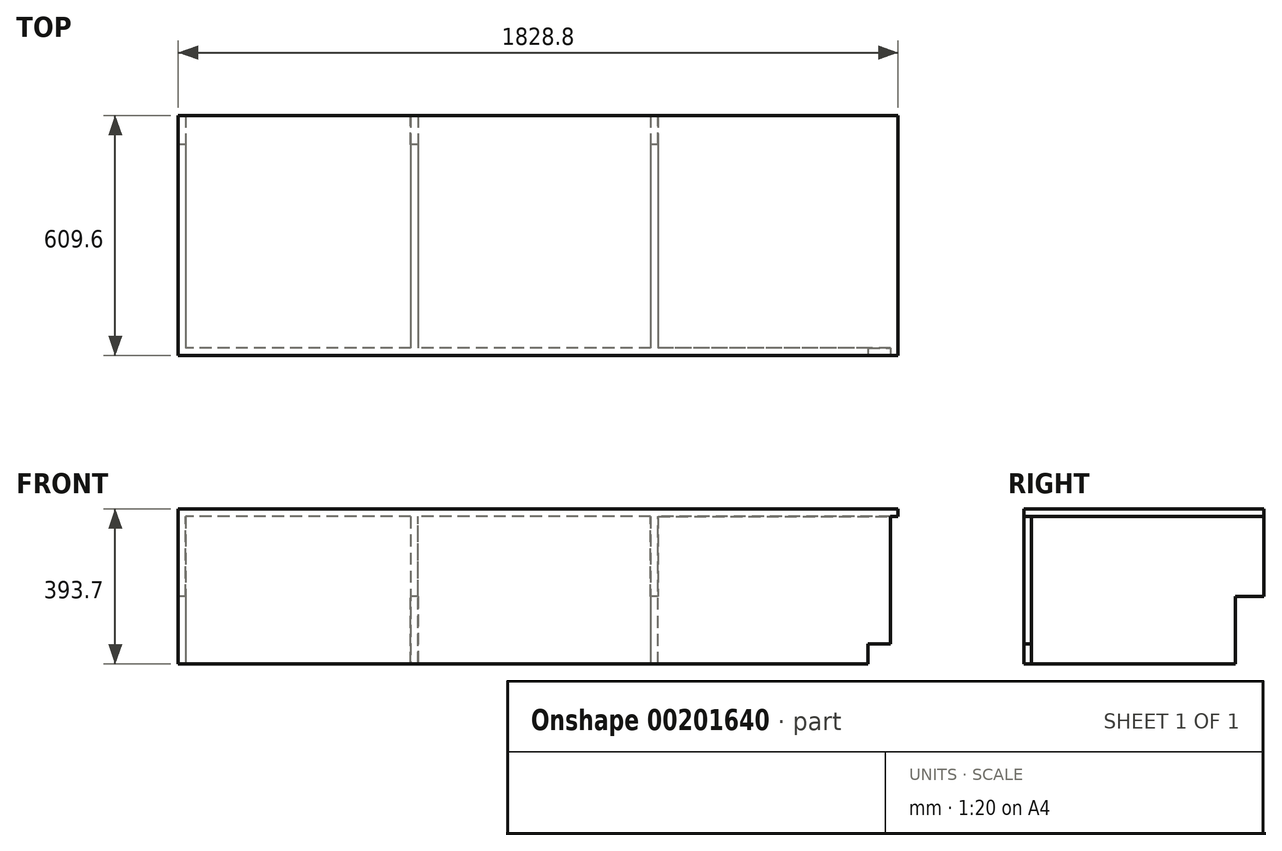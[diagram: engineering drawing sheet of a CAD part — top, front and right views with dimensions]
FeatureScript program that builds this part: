
annotation { "Feature Type Name" : "Feature", "Feature Type Description" : "" }
export const myFeature = defineFeature(function(context is Context, id is Id, definition is map)
    precondition{}
    {
        {
            var Q0;
            Q0=qCreatedBy(makeId("Front.planeOp"),FACE);
            var sketch = newSketch(context, id + "F0", { "sketchPlane" : qUnion([Q0])});
            skLineSegment(sketch, "E0", {"start": v(0, 0) * mm, "end": v(0, 50.8) * mm});
            skLineSegment(sketch, "E1", {"start": v(0, 50.8) * mm, "end": v(76.2, 50.8) * mm});
            skLineSegment(sketch, "E2", {"start": v(76.2, 50.8) * mm, "end": v(76.2, 374.65) * mm});
            skLineSegment(sketch, "E3", {"start": v(0, 0) * mm, "end": v(-1752.6, 0) * mm});
            skLineSegment(sketch, "E4", {"start": v(-1752.6, 0) * mm, "end": v(-1752.6, 374.65) * mm});
            skLineSegment(sketch, "E5.bottom", {"start": v(-1752.6, 374.65) * mm, "end": v(76.2, 374.65) * mm});
            skLineSegment(sketch, "E5.top", {"start": v(-1752.6, 393.7) * mm, "end": v(76.2, 393.7) * mm});
            skLineSegment(sketch, "E5.left", {"start": v(-1752.6, 374.65) * mm, "end": v(-1752.6, 393.7) * mm});
            skLineSegment(sketch, "E5.right", {"start": v(76.2, 374.65) * mm, "end": v(76.2, 393.7) * mm});
            skLineSegment(sketch, "E6.bottom", {"start": v(76.2, 374.65) * mm, "end": v(57.15, 374.65) * mm});
            skLineSegment(sketch, "E6.top", {"start": v(76.2, 50.8) * mm, "end": v(57.15, 50.8) * mm});
            skLineSegment(sketch, "E6.left", {"start": v(76.2, 374.65) * mm, "end": v(76.2, 50.8) * mm});
            skLineSegment(sketch, "E6.right", {"start": v(57.15, 374.65) * mm, "end": v(57.15, 50.8) * mm});
            skLineSegment(sketch, "E7", {"start": v(-533.4, 374.65) * mm, "end": v(-533.4, 0) * mm});
            skLineSegment(sketch, "E8", {"start": v(-533.4, 0) * mm, "end": v(-552.45, 0) * mm});
            skLineSegment(sketch, "E9", {"start": v(-552.45, 0) * mm, "end": v(-552.45, 374.65) * mm});
            skLineSegment(sketch, "E10", {"start": v(-1143, 0) * mm, "end": v(-1143, 374.65) * mm});
            skLineSegment(sketch, "E11", {"start": v(-1162.05, 374.65) * mm, "end": v(-1162.05, 0) * mm});
            skLineSegment(sketch, "E12", {"start": v(-1733.55, 0) * mm, "end": v(-1733.55, 374.65) * mm});
            skSolve(sketch);
        }
        {
            var Q0;
            {var subQ0=sQuery(id+"F0.wireOp",EDGE,"E4");Q0=makeQuery(id+"F0.imprint","IMPRINT",FACE,{"disambiguationData":[TD([[makeQuery(id+"F0.imprint","IMPRINT",EDGE,{"derivedFrom":subQ0}),-1.0]])]});}
            var Q1;
            Q1=makeQuery(id+"F0.imprint","IMPRINT",FACE,{"disambiguationData":[TD([[makeQuery(id+"F0.imprint","IMPRINT",EDGE,{"derivedFrom":sQuery(id+"F0.wireOp",EDGE,"E5.top")}),-1.0]])]});
            var Q2;
            {var subQ0=sQuery(id+"F0.wireOp",EDGE,"E10");Q2=makeQuery(id+"F0.imprint","IMPRINT",FACE,{"disambiguationData":[TD([[makeQuery(id+"F0.imprint","IMPRINT",EDGE,{"derivedFrom":subQ0}),1.0]])]});}
            var Q3;
            {var subQ0=sQuery(id+"F0.wireOp",EDGE,"E7");Q3=makeQuery(id+"F0.imprint","IMPRINT",FACE,{"disambiguationData":[TD([[makeQuery(id+"F0.imprint","IMPRINT",EDGE,{"derivedFrom":subQ0}),-1.0]])]});}
            var Q4;
            Q4=makeQuery(id+"F0.imprint","IMPRINT",FACE,{"disambiguationData":[TD([[makeQuery(id+"F0.imprint","IMPRINT",EDGE,{"derivedFrom":sQuery(id+"F0.wireOp",EDGE,"E6.bottom")}),1.0]])]});
            extrude(context, id + "F1", {"entities" : qUnion([Q0, Q1, Q2, Q3, Q4]), "oppositeDirection" : true, "depth" : 609.6 * mm});
        }
        {
            var Q0;
            {var subQ0=sQuery(id+"F0.wireOp",EDGE,"E4");Q0=makeQuery(id+"F0.imprint","IMPRINT",FACE,{"disambiguationData":[TD([[makeQuery(id+"F0.imprint","IMPRINT",EDGE,{"derivedFrom":subQ0}),-1.0]])]});}
            var Q1;
            {var subQ0=sQuery(id+"F0.wireOp",EDGE,"E11");Q1=makeQuery(id+"F0.imprint","IMPRINT",FACE,{"disambiguationData":[TD([[makeQuery(id+"F0.imprint","IMPRINT",EDGE,{"derivedFrom":subQ0}),-1.0]])]});}
            var Q2;
            Q2=makeQuery(id+"F0.imprint","IMPRINT",FACE,{"disambiguationData":[TD([[makeQuery(id+"F0.imprint","IMPRINT",EDGE,{"derivedFrom":sQuery(id+"F0.wireOp",EDGE,"E5.top")}),-1.0]])]});
            var Q3;
            {var subQ0=sQuery(id+"F0.wireOp",EDGE,"E9");Q3=makeQuery(id+"F0.imprint","IMPRINT",FACE,{"disambiguationData":[TD([[makeQuery(id+"F0.imprint","IMPRINT",EDGE,{"derivedFrom":subQ0}),1.0]])]});}
            var Q4;
            {var subQ0=sQuery(id+"F0.wireOp",EDGE,"E7");Q4=makeQuery(id+"F0.imprint","IMPRINT",FACE,{"disambiguationData":[TD([[makeQuery(id+"F0.imprint","IMPRINT",EDGE,{"derivedFrom":subQ0}),-1.0]])]});}
            var Q5;
            {var subQ4=sQuery(id+"F0.wireOp",EDGE,"E0");Q5=makeQuery(id+"F0.imprint","IMPRINT",FACE,{"disambiguationData":[TD([[makeQuery(id+"F0.imprint","IMPRINT",EDGE,{"derivedFrom":subQ4}),1.0]])]});}
            var Q6;
            Q6=makeQuery(id+"F0.imprint","IMPRINT",FACE,{"disambiguationData":[TD([[makeQuery(id+"F0.imprint","IMPRINT",EDGE,{"derivedFrom":sQuery(id+"F0.wireOp",EDGE,"E6.bottom")}),1.0]])]});
            extrude(context, id + "F2", {"entities" : qUnion([Q0, Q1, Q2, Q3, Q4, Q5, Q6]), "operationType" : NewBodyOperationType.ADD, "oppositeDirection" : true, "depth" : 19.05 * mm});
        }
        {
            var Q0;
            Q0=makeQuery(id+"F1.opExtrude","SWEPT_FACE",FACE,{"disambiguationData":[OSD([sQuery(id+"F0.wireOp",EDGE,"E4"),sQuery(id+"F0.wireOp",EDGE,"E5.left")])]});
            var sketch = newSketch(context, id + "F3", { "sketchPlane" : qUnion([Q0])});
            skLineSegment(sketch, "E13", {"start": v(-609.6, 0) * mm, "end": v(-536.58, 0) * mm});
            skLineSegment(sketch, "E14", {"start": v(-536.58, 0) * mm, "end": v(-536.58, 171.45) * mm});
            skLineSegment(sketch, "E15", {"start": v(-536.58, 171.45) * mm, "end": v(-609.6, 171.45) * mm});
            skSolve(sketch);
        }
        {
            var Q0;
            {var subQ0=sQuery(id+"F3.wireOp",EDGE,"E13");Q0=makeQuery(id+"F3.imprint","IMPRINT",FACE,{"disambiguationData":[TD([[makeQuery(id+"F3.imprint","IMPRINT",EDGE,{"derivedFrom":subQ0}),1.0]])]});}
            var Q1;
            Q1=makeQuery(id+"F1.opExtrude","SWEPT_FACE",FACE,{"disambiguationData":[OSD([sQuery(id+"F0.wireOp",EDGE,"E5.right"),sQuery(id+"F0.wireOp",EDGE,"E6.left")])]});
            extrude(context, id + "F4", {"entities" : qUnion([Q0]), "operationType" : NewBodyOperationType.REMOVE, "endBound" : BoundingType.UP_TO_SURFACE, "oppositeDirection" : true, "endBoundEntityFace" : qUnion([Q1]), "depth" : 25.4 * mm});
        }
    });
